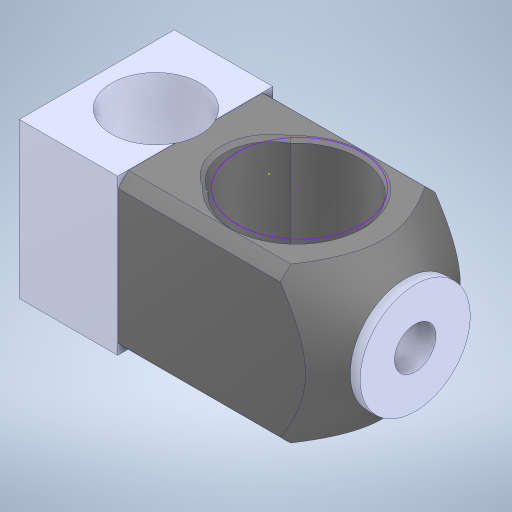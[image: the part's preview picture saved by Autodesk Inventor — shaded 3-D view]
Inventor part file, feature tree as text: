
AUTODESK INVENTOR PART (.ipt)
format: ipt  version: 2023 (Build 270158000, 158)  size: 339,456 bytes
history: mixed  units: in
note: dims shown in document units (in); Inventor stores cm internally (conversion verified against a paired STEP export)
features: sketch x8, extrude x7, other x1, imported_body x1
ambient origin geometry x8: Origin, YZ Plane, XZ Plane, XY Plane, X Axis, Y Axis, Z Axis, Center Point
bodies: Solid1 (imported_parasolid)
feature tree (17):
  other  "6669-001-1-solid1"
  extrude  "Extrusion1"  Depth=0.3937in
  sketch  "Sketch2"  dims[d8=0.3937in d9=0.0in d10=0.0in d11=0.0in]
  extrude  "Extrusion4"  TaperAngle=0.0deg  [1 undecoded]
  sketch  "Sketch5"  dims[d16=0.2362in d17=0.1969in]
  extrude  "Extrusion5"  Depth=0.3937in TaperAngle=0.0deg
  extrude  "Extrusion6"  Depth=0.1969in
  extrude  "Extrusion7"  Depth=0.3543in
  extrude  "Extrusion8"  Depth=0.1654in
  extrude  "Extrusion9"  Depth=0.0344in
  sketch  "Sketch1"  dims[d0=0.3937in d1=0.0in d7=0.1654in]
  sketch  "Sketch4"  dims[d12=0.0394in d13=0.0in d14=0.3937in d15=0.0in]
  sketch  "Sketch6"  dims[d18=0.1969in d19=0.0in d20=0.3543in]
  sketch  "Sketch7"  dims[d21=0.0in d22=0.0in d23=0.1654in]
  sketch  "Sketch8"  dims[d2=0.0197in d3=0.0344in]
  sketch  "Sketch9"  dims[d4=0.0197in d5=0.0344in]
  imported_body  NMx_Import_Brep_tag  [imported B-rep: ~14 faces, bbox_mm=[22.836, 10.765997, 12.379599]]
note: 1 required parameter value undecoded (feature->parameter linkage not recoverable at this tier; creation-order binding heuristic only, values carry confidence <= 0.55)
